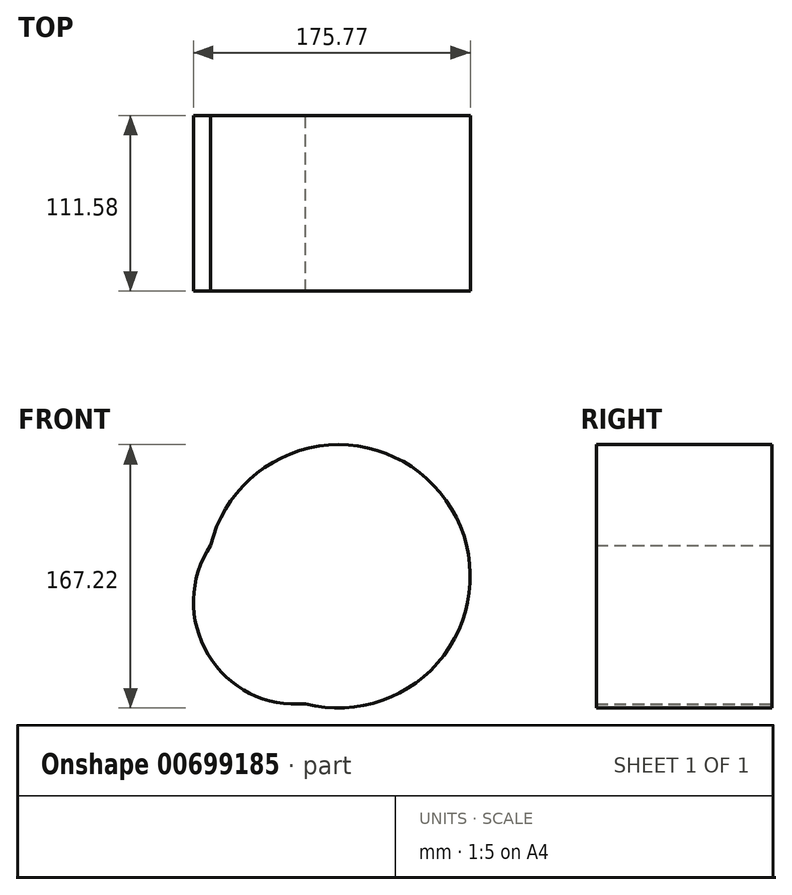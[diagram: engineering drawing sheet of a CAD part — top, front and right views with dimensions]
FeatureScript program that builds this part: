
annotation { "Feature Type Name" : "Feature", "Feature Type Description" : "" }
export const myFeature = defineFeature(function(context is Context, id is Id, definition is map)
    precondition{}
    {
        {
            var Q0;
            Q0=qCreatedBy(makeId("Front.planeOp"),FACE);
            var sketch = newSketch(context, id + "F0", { "sketchPlane" : qUnion([Q0])});
            skArc(sketch, "E0", {"start": v(-54, 36) * mm, "mid": v(-55.69, -33.32) * mm, "end": v(6.2, -64.6) * mm});
            skArc(sketch, "E1", {"start": v(6.2, -64.6) * mm, "mid": v(99, 59.24) * mm, "end": v(-54, 36) * mm});
            skSolve(sketch);
        }
        {
            var Q0;
            Q0 = qSketchRegion(id + "F0", true);
            extrude(context, id + "F1", {"entities" : qUnion([Q0]), "depth" : 111.58 * mm, "offsetDistance" : 25.4 * mm});
        }
    });
